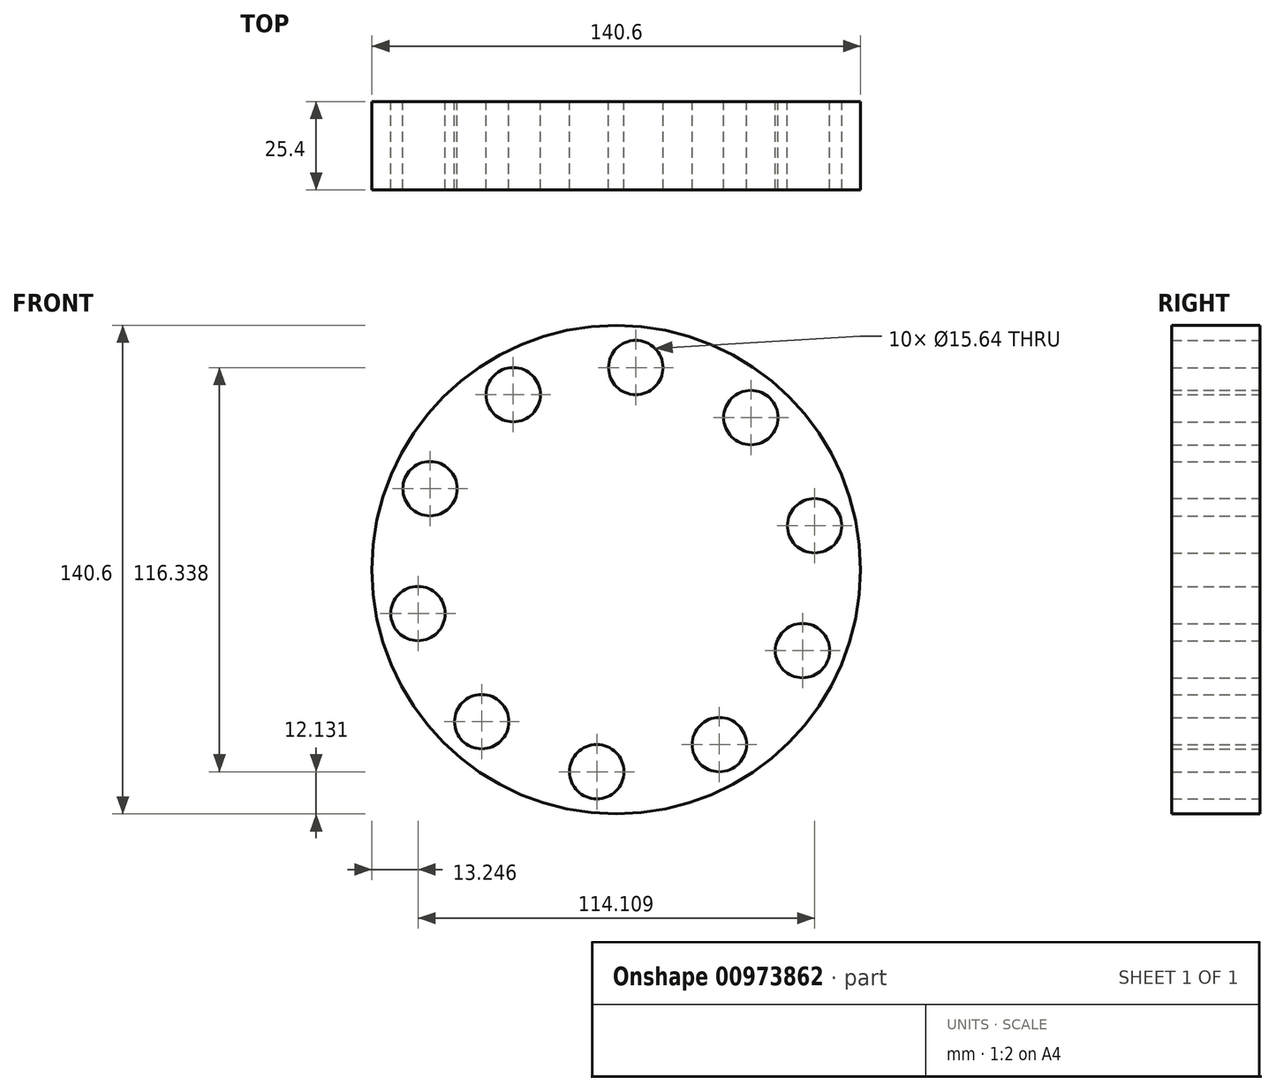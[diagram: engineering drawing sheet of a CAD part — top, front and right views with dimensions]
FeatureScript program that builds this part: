
annotation { "Feature Type Name" : "Feature", "Feature Type Description" : "" }
export const myFeature = defineFeature(function(context is Context, id is Id, definition is map)
    precondition{}
    {
        {
            var Q0;
            Q0=qCreatedBy(makeId("Front.planeOp"),FACE);
            var sketch = newSketch(context, id + "F0", { "sketchPlane" : qUnion([Q0])});
            skLineSegment(sketch, "E0.top", {"start": v(-35.2, -121.82) * mm, "end": v(137.92, -121.82) * mm});
            skLineSegment(sketch, "E0.right", {"start": v(137.92, 0) * mm, "end": v(137.92, -121.82) * mm});
            skCircle(sketch, "E1", {"center": v(0, 0) * mm, "radius": 70.3 * mm});
            skCircle(sketch, "E2", {"center": v(-29.65, 50.36) * mm, "radius": 7.82 * mm});
            skCircle(sketch, "E3.1.0", {"center": v(-53.59, 23.3) * mm, "radius": 7.82 * mm});
            skCircle(sketch, "E3.2.0", {"center": v(-57.05, -12.64) * mm, "radius": 7.82 * mm});
            skCircle(sketch, "E3.3.0", {"center": v(-38.73, -43.76) * mm, "radius": 7.82 * mm});
            skCircle(sketch, "E3.4.0", {"center": v(-5.6, -58.17) * mm, "radius": 7.82 * mm});
            skCircle(sketch, "E3.5.0", {"center": v(29.65, -50.36) * mm, "radius": 7.82 * mm});
            skCircle(sketch, "E3.6.0", {"center": v(53.59, -23.3) * mm, "radius": 7.82 * mm});
            skCircle(sketch, "E3.7.0", {"center": v(57.05, 12.64) * mm, "radius": 7.82 * mm});
            skCircle(sketch, "E3.8.0", {"center": v(38.73, 43.76) * mm, "radius": 7.82 * mm});
            skCircle(sketch, "E3.9.0", {"center": v(5.6, 58.17) * mm, "radius": 7.82 * mm});
            skSolve(sketch);
        }
        {
            var Q0;
            Q0 = qSketchRegion(id + "F0", true);
            extrude(context, id + "F1", {"entities" : qUnion([Q0]), "depth" : 25.4 * mm, "offsetDistance" : 25.4 * mm});
        }
    });
